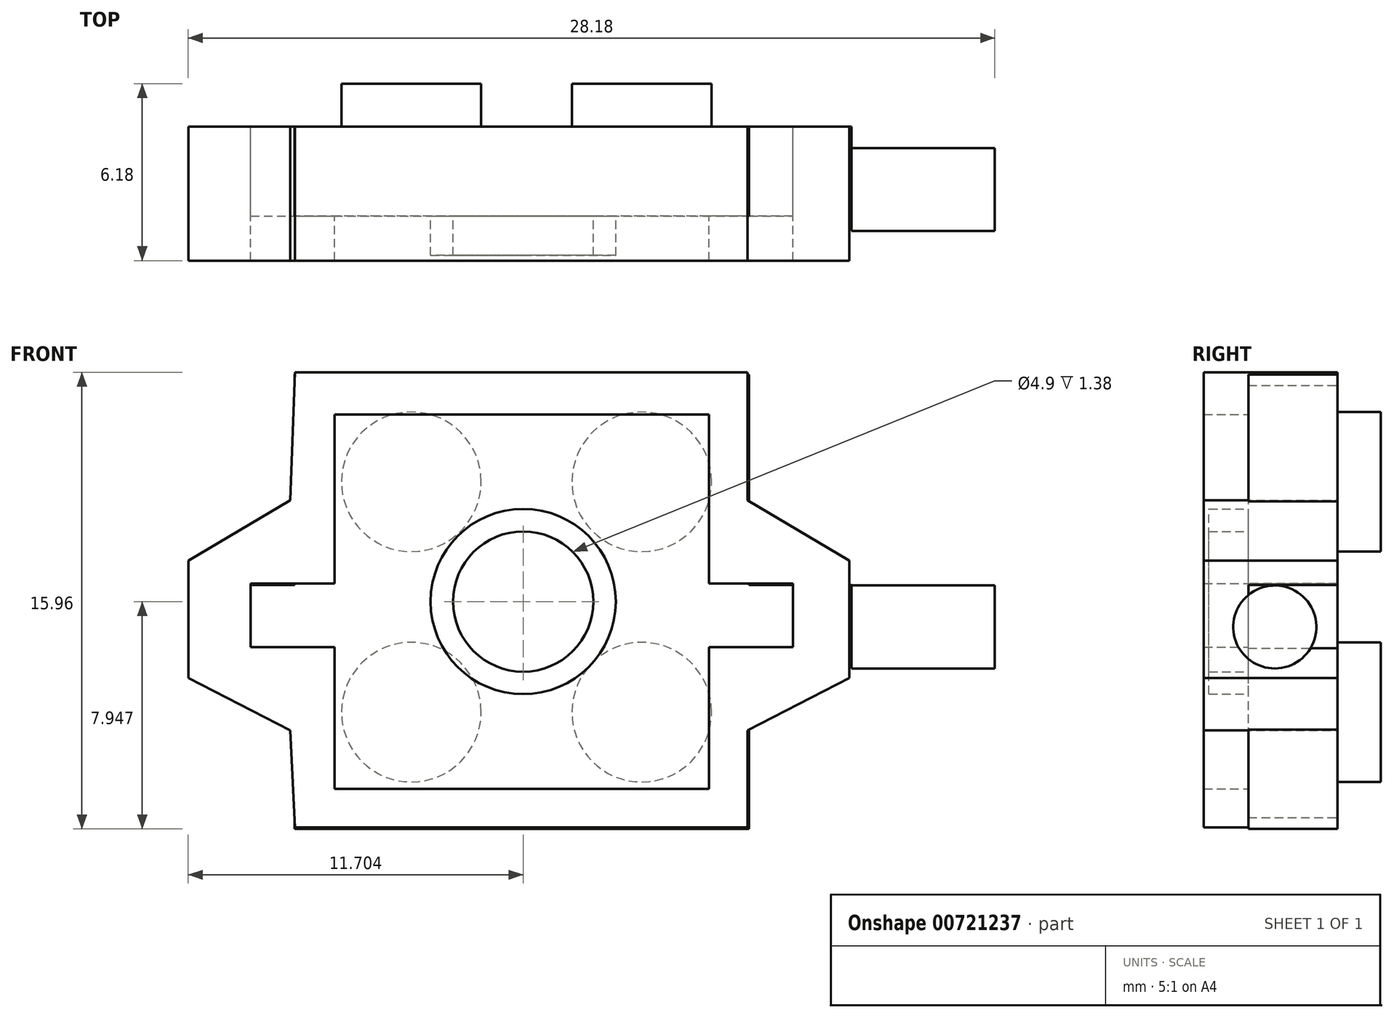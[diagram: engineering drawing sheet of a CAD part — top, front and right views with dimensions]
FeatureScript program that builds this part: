
annotation { "Feature Type Name" : "Feature", "Feature Type Description" : "" }
export const myFeature = defineFeature(function(context is Context, id is Id, definition is map)
    precondition{}
    {
        {
            var Q0;
            Q0=qCreatedBy(makeId("Front.planeOp"),FACE);
            var sketch = newSketch(context, id + "F0", { "sketchPlane" : qUnion([Q0])});
            skLineSegment(sketch, "E0.bottom", {"start": v(-0.9, 12.43) * mm, "end": v(14.99, 12.43) * mm});
            skLineSegment(sketch, "E0.top", {"start": v(-0.9, -3.45) * mm, "end": v(14.99, -3.45) * mm});
            skLineSegment(sketch, "E0.left", {"start": v(-0.9, 12.43) * mm, "end": v(-0.9, 5.63) * mm});
            skLineSegment(sketch, "E0.right", {"start": v(14.99, 12.43) * mm, "end": v(14.99, 5.55) * mm});
            skLineSegment(sketch, "E1.trimOffspring", {"start": v(14.99, 2.86) * mm, "end": v(14.99, -3.45) * mm});
            skPoint(sketch, "E2.end.orphan", {"position": v(13.33, 5.55) * mm});
            skLineSegment(sketch, "E3", {"start": v(12.79, 5.55) * mm, "end": v(13.33, 5.55) * mm});
            skLineSegment(sketch, "E4.trimOffspring", {"start": v(-0.9, 2.86) * mm, "end": v(-0.9, -3.45) * mm});
            skPoint(sketch, "E5.start.orphan", {"position": v(12.79, 3.35) * mm});
            skLineSegment(sketch, "E6.bottom", {"start": v(-3.76, 2.86) * mm, "end": v(-0.9, 2.86) * mm});
            skLineSegment(sketch, "E6.top", {"start": v(-3.76, 5.07) * mm, "end": v(-0.9, 5.07) * mm});
            skLineSegment(sketch, "E6.left", {"start": v(-3.76, 2.86) * mm, "end": v(-3.76, 5.07) * mm});
            skLineSegment(sketch, "E7.bottom", {"start": v(14.99, 2.86) * mm, "end": v(18.57, 2.86) * mm});
            skLineSegment(sketch, "E7.top", {"start": v(14.99, 5.07) * mm, "end": v(18.57, 5.07) * mm});
            skLineSegment(sketch, "E7.right", {"start": v(18.57, 2.86) * mm, "end": v(18.57, 5.07) * mm});
            skLineSegment(sketch, "E8", {"start": v(-0.9, 5.63) * mm, "end": v(-0.9, 5.07) * mm});
            skPoint(sketch, "E9.orphan", {"position": v(1.3, 5.07) * mm});
            skPoint(sketch, "E10.end.orphan", {"position": v(1.3, 2.86) * mm});
            skPoint(sketch, "E6.right.end.orphan", {"position": v(1.3, 3.35) * mm});
            skPoint(sketch, "E7.left.start.orphan", {"position": v(12.79, 2.86) * mm});
            skLineSegment(sketch, "E11", {"start": v(14.99, 5.55) * mm, "end": v(14.99, 5.07) * mm});
            skSolve(sketch);
        }
        {
            var Q0;
            Q0 = qSketchRegion(id + "F0", true);
            extrude(context, id + "F1", {"entities" : qUnion([Q0]), "depth" : 3.12 * mm, "offsetDistance" : 25 * mm});
        }
        {
            var Q0;
            Q0=qCreatedBy(makeId("Front.planeOp"),FACE);
            var sketch = newSketch(context, id + "F2", { "sketchPlane" : qUnion([Q0])});
            skCircle(sketch, "E12", {"center": v(11.24, 8.68) * mm, "radius": 2.44 * mm});
            skCircle(sketch, "E13", {"center": v(3.19, 8.68) * mm, "radius": 2.44 * mm});
            skCircle(sketch, "E14", {"center": v(3.19, 0.63) * mm, "radius": 2.44 * mm});
            skCircle(sketch, "E15", {"center": v(11.24, 0.63) * mm, "radius": 2.44 * mm});
            skSolve(sketch);
        }
        {
            var Q0;
            Q0 = qSketchRegion(id + "F2", true);
            extrude(context, id + "F3", {"entities" : qUnion([Q0]), "operationType" : NewBodyOperationType.ADD, "oppositeDirection" : true, "depth" : 1.5 * mm, "offsetDistance" : 25 * mm});
        }
        {
            var Q0;
            Q0=qCreatedBy(makeId("Front.planeOp"),FACE);
            var sketch = newSketch(context, id + "F4", { "sketchPlane" : qUnion([Q0])});
            skCircle(sketch, "E16", {"center": v(7.05, 4.5) * mm, "radius": 3.27 * mm});
            skCircle(sketch, "E17", {"center": v(7.05, 4.5) * mm, "radius": 2.41 * mm});
            skLineSegment(sketch, "E18.bottom", {"start": v(0.5, 11.03) * mm, "end": v(13.59, 11.03) * mm});
            skLineSegment(sketch, "E18.top", {"start": v(0.5, -2.05) * mm, "end": v(13.59, -2.05) * mm});
            skLineSegment(sketch, "E18.right", {"start": v(13.59, 11.03) * mm, "end": v(13.59, 5.13) * mm});
            skPoint(sketch, "E19.center.orphan", {"position": v(3.2, 8.9) * mm});
            skPoint(sketch, "E20.center.orphan", {"position": v(3.2, 0) * mm});
            skLineSegment(sketch, "E21", {"start": v(0.5, 11.03) * mm, "end": v(0.5, 5.13) * mm});
            skPoint(sketch, "E22.orphan", {"position": v(0, 11.03) * mm});
            skLineSegment(sketch, "E23.bottom", {"start": v(13.59, 5.13) * mm, "end": v(16.52, 5.13) * mm});
            skLineSegment(sketch, "E23.top", {"start": v(13.59, 2.9) * mm, "end": v(16.52, 2.9) * mm});
            skLineSegment(sketch, "E23.right", {"start": v(16.52, 5.13) * mm, "end": v(16.52, 2.9) * mm});
            skLineSegment(sketch, "E24.bottom", {"start": v(0.5, 5.13) * mm, "end": v(-2.42, 5.13) * mm});
            skLineSegment(sketch, "E24.top", {"start": v(0.5, 2.9) * mm, "end": v(-2.42, 2.9) * mm});
            skLineSegment(sketch, "E24.right", {"start": v(-2.42, 5.13) * mm, "end": v(-2.42, 2.9) * mm});
            skLineSegment(sketch, "E25.trimOffspring", {"start": v(0.5, 2.9) * mm, "end": v(0.5, -2.05) * mm});
            skLineSegment(sketch, "E26.trimOffspring", {"start": v(13.59, 2.9) * mm, "end": v(13.59, -2.05) * mm});
            skLineSegment(sketch, "E27", {"start": v(18.5, 5.93) * mm, "end": v(18.5, 1.83) * mm});
            skLineSegment(sketch, "E28.bottom", {"start": v(-0.88, 12.5) * mm, "end": v(14.93, 12.5) * mm});
            skLineSegment(sketch, "E28.top", {"start": v(-0.88, -3.39) * mm, "end": v(14.93, -3.39) * mm});
            skLineSegment(sketch, "E28.right", {"start": v(14.93, 12.5) * mm, "end": v(14.93, -3.39) * mm});
            skLineSegment(sketch, "E29", {"start": v(18.5, 1.83) * mm, "end": v(14.93, 0) * mm});
            skLineSegment(sketch, "E30", {"start": v(18.5, 5.93) * mm, "end": v(14.93, 8.03) * mm});
            skLineSegment(sketch, "E31.MirrorCS", {"start": v(-4.6, 5.93) * mm, "end": v(-1.05, 8.03) * mm});
            skLineSegment(sketch, "E32.MirrorCS", {"start": v(-4.6, 1.83) * mm, "end": v(-1.05, 0) * mm});
            skLineSegment(sketch, "E33.MirrorCS", {"start": v(-4.6, 5.93) * mm, "end": v(-4.6, 1.83) * mm});
            skLineSegment(sketch, "E34", {"start": v(-0.88, 12.5) * mm, "end": v(-1.05, 8.03) * mm});
            skLineSegment(sketch, "E35", {"start": v(-0.88, -3.39) * mm, "end": v(-1.05, 0) * mm});
            skSolve(sketch);
        }
        {
            var Q0;
            Q0 = qSketchRegion(id + "F4", true);
            extrude(context, id + "F5", {"entities" : qUnion([Q0]), "operationType" : NewBodyOperationType.ADD, "depth" : 4.68 * mm, "offsetDistance" : 25 * mm});
        }
        {
            var Q0;
            Q0=qCreatedBy(makeId("Front.planeOp"),FACE);
            var sketch = newSketch(context, id + "F6", { "sketchPlane" : qUnion([Q0])});
            skCircle(sketch, "E36", {"center": v(7.1, 4.5) * mm, "radius": 3.23 * mm});
            skCircle(sketch, "E37", {"center": v(7.1, 4.5) * mm, "radius": 2.45 * mm});
            skSolve(sketch);
        }
        {
            var Q0;
            Q0 = qSketchRegion(id + "F6", true);
            extrude(context, id + "F7", {"entities" : qUnion([Q0]), "operationType" : NewBodyOperationType.ADD, "depth" : 4.5 * mm, "offsetDistance" : 25 * mm});
        }
        {
            var Q0;
            Q0=makeQuery(id+"F1.opExtrude","SWEPT_FACE",FACE,{"disambiguationData":[OSD([sQuery(id+"F0.wireOp",EDGE,"E7.right")])]});
            var sketch = newSketch(context, id + "F8", { "sketchPlane" : qUnion([Q0])});
            skLineSegment(sketch, "E38", {"start": v(-4.37, 5.5) * mm, "end": v(0, 1.7) * mm, "construction": true});
            skLineSegment(sketch, "E39", {"start": v(0, 5.55) * mm, "end": v(-4.25, 1.8) * mm});
            skCircle(sketch, "E40", {"center": v(-2.2, 3.6) * mm, "radius": 1.45 * mm});
            skSolve(sketch);
        }
        {
            var Q0;
            Q0 = qSketchRegion(id + "F8", true);
            extrude(context, id + "F9", {"entities" : qUnion([Q0]), "operationType" : NewBodyOperationType.ADD, "depth" : 5 * mm, "offsetDistance" : 25 * mm});
        }
        {
            var Q0;
            Q0=makeQuery(id+"F5.opExtrude","SWEPT_FACE",FACE,{"disambiguationData":[OSD([sQuery(id+"F4.wireOp",EDGE,"E33.MirrorCS")])]});
            var sketch = newSketch(context, id + "F10", { "sketchPlane" : qUnion([Q0])});
            skLineSegment(sketch, "E41", {"start": v(0, 5.93) * mm, "end": v(4.68, 1.83) * mm, "construction": true});
            skLineSegment(sketch, "E42", {"start": v(4.68, 5.93) * mm, "end": v(0, 1.83) * mm, "construction": true});
            skCircle(sketch, "E43", {"center": v(2.34, 3.88) * mm, "radius": 1.45 * mm});
            skSolve(sketch);
        }
        {
            var Q0;
            Q0 = qConstructionFilter(qBodyType(qCreatedBy(id + "F10" ,EDGE), BodyType.WIRE), ConstructionObject.NO);
            extrude(context, id + "F11", {"bodyType" : ToolBodyType.SURFACE, "surfaceEntities" : qUnion([Q0]), "depth" : 5 * mm, "offsetDistance" : 25 * mm});
        }
    });
